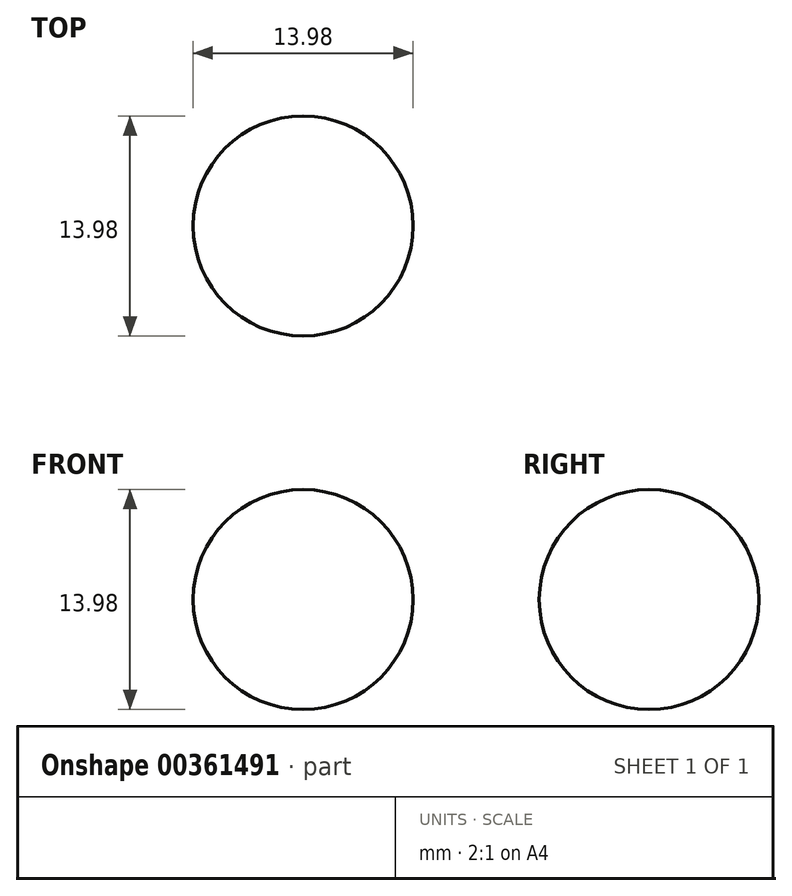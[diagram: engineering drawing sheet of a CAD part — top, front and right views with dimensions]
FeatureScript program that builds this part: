
annotation { "Feature Type Name" : "Feature", "Feature Type Description" : "" }
export const myFeature = defineFeature(function(context is Context, id is Id, definition is map)
    precondition{}
    {
        {
            var Q0;
            Q0=qCreatedBy(makeId("Front.planeOp"),FACE);
            var sketch = newSketch(context, id + "F0", { "sketchPlane" : qUnion([Q0])});
            skCircle(sketch, "E0", {"center": v(0, 0) * mm, "radius": 6.99 * mm});
            skLineSegment(sketch, "E1", {"start": v(0, 6.98) * mm, "end": v(0, -6.98) * mm});
            skSolve(sketch);
        }
        {
            var Q0;
            {var subQ0=sQuery(id+"F0.wireOp",EDGE,"E1");Q0=makeQuery(id+"F0.imprint","IMPRINT",FACE,{"disambiguationData":[TD([[makeQuery(id+"F0.imprint","IMPRINT",EDGE,{"derivedFrom":subQ0}),1.0]])]});}
            var Q1;
            Q1=sQuery(id+"F0.wireOp",EDGE,"E1");
            revolve(context, id + "F1", {"entities" : qUnion([Q0]), "axis" : qUnion([Q1]), "revolveType" : RevolveType.FULL});
        }
    });
